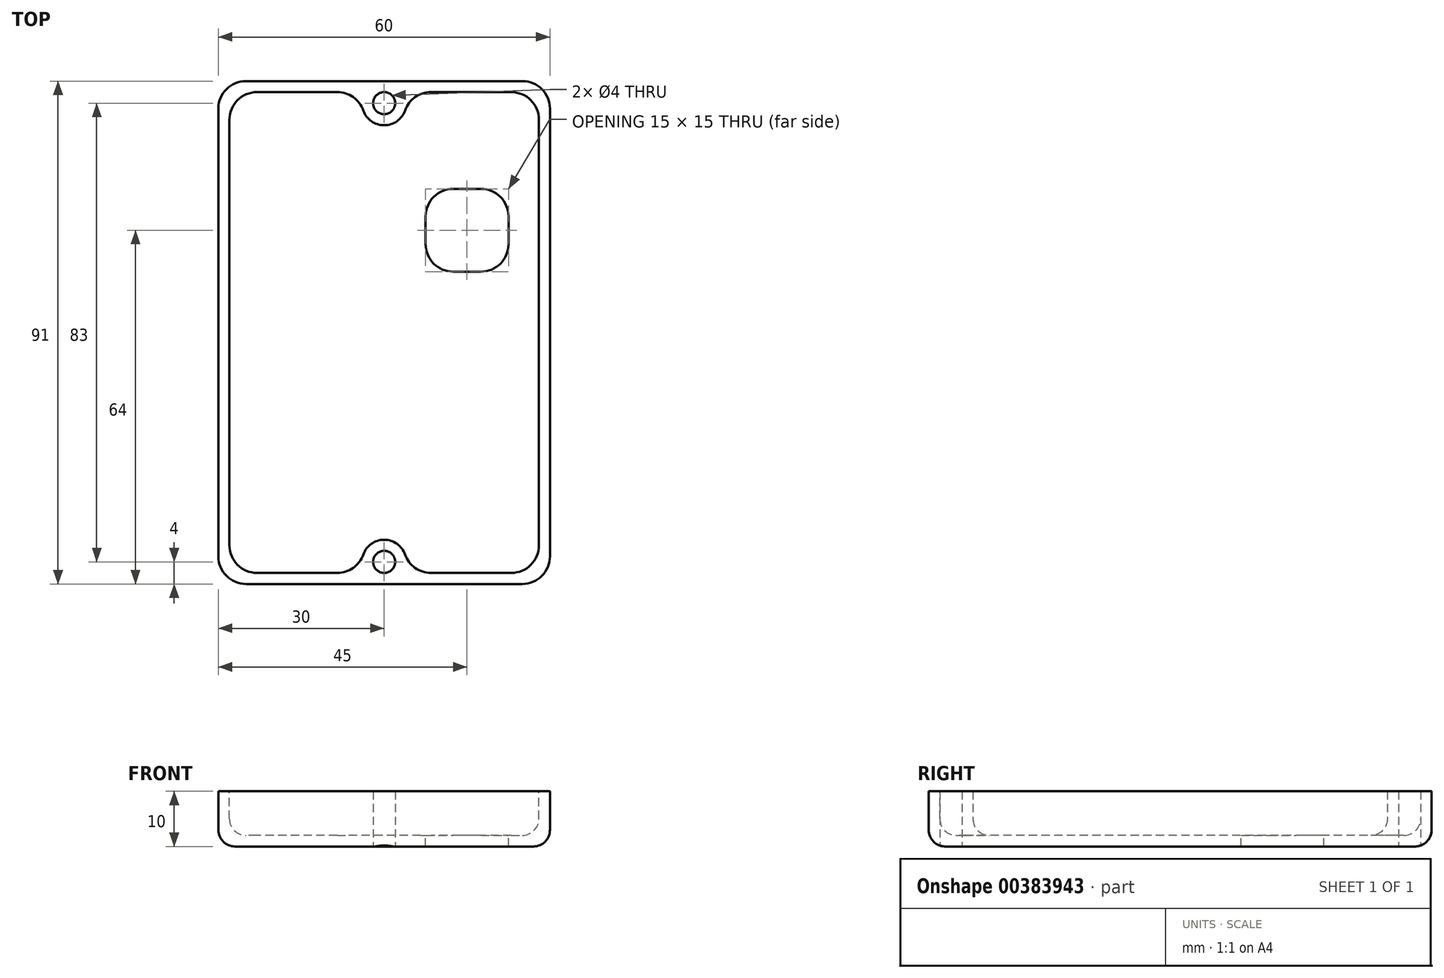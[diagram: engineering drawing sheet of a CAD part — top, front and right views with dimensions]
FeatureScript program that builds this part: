
annotation { "Feature Type Name" : "Feature", "Feature Type Description" : "" }
export const myFeature = defineFeature(function(context is Context, id is Id, definition is map)
    precondition{}
    {
        {
            assignVariable(context, id + "F0", {"name" : "lidwallthickness", "anyValue" : 2});
        }
        {
            assignVariable(context, id + "F1", {"name" : "lidheight", "anyValue" : 10});
        }
        {
            assignVariable(context, id + "F2", {"name" : "filletradius", "anyValue" : 3});
        }
        {
            var Q0;
            Q0=qCreatedBy(makeId("Top.planeOp"),FACE);
            var sketch = newSketch(context, id + "F3", { "sketchPlane" : qUnion([Q0])});
            skLineSegment(sketch, "E0.bottom", {"start": v(30, 45.5) * mm, "end": v(-30, 45.5) * mm});
            skLineSegment(sketch, "E0.top", {"start": v(30, -45.5) * mm, "end": v(-30, -45.5) * mm});
            skLineSegment(sketch, "E0.left", {"start": v(30, 45.5) * mm, "end": v(30, -45.5) * mm});
            skLineSegment(sketch, "E0.right", {"start": v(-30, 45.5) * mm, "end": v(-30, -45.5) * mm});
            skPoint(sketch, "E0.middle", {"position": v(0, 0) * mm});
            skSolve(sketch);
        }
        {
            var Q0;
            Q0=qSketchRegion(id+"F3",true);
            extrude(context, id + "F4", {"entities" : qUnion([Q0]), "depth" : (getVariable(context, 'lidheight')) * mm});
        }
        {
            var Q0;
            Q0=makeQuery(id+"F4.opExtrude","CAP_FACE",FACE,{"disambiguationData":[OSD([sQuery(id+"F3.wireOp",EDGE,"E0.bottom"),sQuery(id+"F3.wireOp",EDGE,"E0.top"),sQuery(id+"F3.wireOp",EDGE,"E0.left"),sQuery(id+"F3.wireOp",EDGE,"E0.right")])],"isStart":false});
            var sketch = newSketch(context, id + "F5", { "sketchPlane" : qUnion([Q0])});
            skLineSegment(sketch, "E1.bottom", {"start": v(28, 43.5) * mm, "end": v(-28, 43.5) * mm});
            skLineSegment(sketch, "E1.top", {"start": v(28, -43.5) * mm, "end": v(-28, -43.5) * mm});
            skLineSegment(sketch, "E1.left", {"start": v(28, 43.5) * mm, "end": v(28, -43.5) * mm});
            skLineSegment(sketch, "E1.right", {"start": v(-28, 43.5) * mm, "end": v(-28, -43.5) * mm});
            skPoint(sketch, "E1.middle", {"position": v(0, 0) * mm});
            skSolve(sketch);
        }
        {
            var Q0;
            Q0=qSketchRegion(id+"F5",true);
            extrude(context, id + "F6", {"entities" : qUnion([Q0]), "operationType" : NewBodyOperationType.REMOVE, "oppositeDirection" : true, "depth" : (getVariable(context, 'lidheight') - getVariable(context, 'lidwallthickness')) * mm});
        }
        {
            var Q0;
            Q0=makeQuery(id+"F4.opExtrude","CAP_FACE",FACE,{"disambiguationData":[OSD([sQuery(id+"F3.wireOp",EDGE,"E0.bottom"),sQuery(id+"F3.wireOp",EDGE,"E0.top"),sQuery(id+"F3.wireOp",EDGE,"E0.left"),sQuery(id+"F3.wireOp",EDGE,"E0.right")])],"isStart":true});
            var sketch = newSketch(context, id + "F7", { "sketchPlane" : qUnion([Q0])});
            skCircle(sketch, "E2", {"center": v(0, -41.5) * mm, "radius": 4 * mm});
            skCircle(sketch, "E3.MirrorC", {"center": v(0, 41.5) * mm, "radius": 4 * mm});
            skSolve(sketch);
        }
        {
            var Q0;
            Q0=qSketchRegion(id+"F7",true);
            extrude(context, id + "F8", {"entities" : qUnion([Q0]), "operationType" : NewBodyOperationType.ADD, "oppositeDirection" : true, "depth" : (getVariable(context, 'lidheight')) * mm});
        }
        {
            var Q0;
            Q0=makeQuery(id+"F4.opExtrude","CAP_FACE",FACE,{"disambiguationData":[OSD([sQuery(id+"F3.wireOp",EDGE,"E0.bottom"),sQuery(id+"F3.wireOp",EDGE,"E0.top"),sQuery(id+"F3.wireOp",EDGE,"E0.left"),sQuery(id+"F3.wireOp",EDGE,"E0.right")])],"isStart":true});
            var sketch = newSketch(context, id + "F9", { "sketchPlane" : qUnion([Q0])});
            skCircle(sketch, "E4", {"center": v(0, -41.5) * mm, "radius": 2 * mm});
            skPoint(sketch, "E4.centerSnap0", {"position": v(0, -45.5) * mm});
            skCircle(sketch, "E5.MirrorC", {"center": v(0, 41.5) * mm, "radius": 2 * mm});
            skSolve(sketch);
        }
        {
            var Q0;
            Q0=qSketchRegion(id+"F9",true);
            extrude(context, id + "F10", {"entities" : qUnion([Q0]), "operationType" : NewBodyOperationType.REMOVE, "endBound" : BoundingType.THROUGH_ALL, "oppositeDirection" : true, "depth" : 25 * mm});
        }
        {
            var Q0;
            Q0=makeQuery(id+"F8.boolean.opBoolean","INTERSECT",EDGE,{"disambiguationData":[OD(1.0)],"derivedFrom":[makeQuery(id+"F6.boolean.opBoolean","COPY",FACE,{"derivedFrom":makeQuery(id+"F6.opExtrude","SWEPT_FACE",FACE,{"disambiguationData":[OSD([sQuery(id+"F5.wireOp",EDGE,"E1.bottom")])]})}),makeQuery(id+"F8.opExtrude","SWEPT_FACE",FACE,{"disambiguationData":[OSD([sQuery(id+"F7.wireOp",EDGE,"E2")])]})]});
            var Q1;
            Q1=makeQuery(id+"F8.boolean.opBoolean","INTERSECT",EDGE,{"disambiguationData":[OD(0.0)],"derivedFrom":[makeQuery(id+"F6.boolean.opBoolean","COPY",FACE,{"derivedFrom":makeQuery(id+"F6.opExtrude","SWEPT_FACE",FACE,{"disambiguationData":[OSD([sQuery(id+"F5.wireOp",EDGE,"E1.bottom")])]})}),makeQuery(id+"F8.opExtrude","SWEPT_FACE",FACE,{"disambiguationData":[OSD([sQuery(id+"F7.wireOp",EDGE,"E2")])]})]});
            var Q2;
            Q2=makeQuery(id+"F8.boolean.opBoolean","INTERSECT",EDGE,{"disambiguationData":[OD(0.0)],"derivedFrom":[makeQuery(id+"F6.boolean.opBoolean","COPY",FACE,{"derivedFrom":makeQuery(id+"F6.opExtrude","SWEPT_FACE",FACE,{"disambiguationData":[OSD([sQuery(id+"F5.wireOp",EDGE,"E1.top")])]})}),makeQuery(id+"F8.opExtrude","SWEPT_FACE",FACE,{"disambiguationData":[OSD([sQuery(id+"F7.wireOp",EDGE,"E3.MirrorC")])]})]});
            var Q3;
            Q3=makeQuery(id+"F8.boolean.opBoolean","INTERSECT",EDGE,{"disambiguationData":[OD(1.0)],"derivedFrom":[makeQuery(id+"F6.boolean.opBoolean","COPY",FACE,{"derivedFrom":makeQuery(id+"F6.opExtrude","SWEPT_FACE",FACE,{"disambiguationData":[OSD([sQuery(id+"F5.wireOp",EDGE,"E1.top")])]})}),makeQuery(id+"F8.opExtrude","SWEPT_FACE",FACE,{"disambiguationData":[OSD([sQuery(id+"F7.wireOp",EDGE,"E3.MirrorC")])]})]});
            fillet(context, id + "F11", {"entities" : qUnion([Q0, Q1, Q2, Q3]), "radius" : 5 * mm, "tangentPropagation" : true, "allowEdgeOverflow" : false});
        }
        {
            var Q0;
            Q0=makeQuery(id+"F4.opExtrude","SWEPT_EDGE",EDGE,{"disambiguationData":[OSD([sQuery(id+"F3.wireOp",EDGE,"E0.top"),sQuery(id+"F3.wireOp",EDGE,"E0.left")])]});
            var Q1;
            Q1=makeQuery(id+"F4.opExtrude","SWEPT_EDGE",EDGE,{"disambiguationData":[OSD([sQuery(id+"F3.wireOp",EDGE,"E0.top"),sQuery(id+"F3.wireOp",EDGE,"E0.right")])]});
            var Q2;
            Q2=makeQuery(id+"F4.opExtrude","SWEPT_EDGE",EDGE,{"disambiguationData":[OSD([sQuery(id+"F3.wireOp",EDGE,"E0.bottom"),sQuery(id+"F3.wireOp",EDGE,"E0.left")])]});
            var Q3;
            Q3=makeQuery(id+"F4.opExtrude","SWEPT_EDGE",EDGE,{"disambiguationData":[OSD([sQuery(id+"F3.wireOp",EDGE,"E0.bottom"),sQuery(id+"F3.wireOp",EDGE,"E0.right")])]});
            var Q4;
            Q4=makeQuery(id+"F6.boolean.opBoolean","COPY",EDGE,{"derivedFrom":makeQuery(id+"F6.opExtrude","SWEPT_EDGE",EDGE,{"disambiguationData":[OSD([sQuery(id+"F5.wireOp",EDGE,"E1.top"),sQuery(id+"F5.wireOp",EDGE,"E1.left")])]})});
            var Q5;
            Q5=makeQuery(id+"F6.boolean.opBoolean","COPY",EDGE,{"derivedFrom":makeQuery(id+"F6.opExtrude","SWEPT_EDGE",EDGE,{"disambiguationData":[OSD([sQuery(id+"F5.wireOp",EDGE,"E1.top"),sQuery(id+"F5.wireOp",EDGE,"E1.right")])]})});
            var Q6;
            Q6=makeQuery(id+"F6.boolean.opBoolean","COPY",EDGE,{"derivedFrom":makeQuery(id+"F6.opExtrude","SWEPT_EDGE",EDGE,{"disambiguationData":[OSD([sQuery(id+"F5.wireOp",EDGE,"E1.bottom"),sQuery(id+"F5.wireOp",EDGE,"E1.right")])]})});
            var Q7;
            Q7=makeQuery(id+"F6.boolean.opBoolean","COPY",EDGE,{"derivedFrom":makeQuery(id+"F6.opExtrude","SWEPT_EDGE",EDGE,{"disambiguationData":[OSD([sQuery(id+"F5.wireOp",EDGE,"E1.bottom"),sQuery(id+"F5.wireOp",EDGE,"E1.left")])]})});
            fillet(context, id + "F12", {"entities" : qUnion([Q0, Q1, Q2, Q3, Q4, Q5, Q6, Q7]), "radius" : 5 * mm, "tangentPropagation" : true, "allowEdgeOverflow" : false});
        }
        {
            var Q0;
            Q0=makeQuery(id+"F6.boolean.opBoolean","COPY",EDGE,{"derivedFrom":makeQuery(id+"F6.opExtrude","CAP_EDGE",EDGE,{"disambiguationData":[OSD([sQuery(id+"F5.wireOp",EDGE,"E1.right")])],"isStart":false})});
            var Q1;
            Q1=makeQuery(id+"F4.opExtrude","CAP_EDGE",EDGE,{"disambiguationData":[OSD([sQuery(id+"F3.wireOp",EDGE,"E0.left")])],"isStart":true});
            fillet(context, id + "F13", {"entities" : qUnion([Q0, Q1]), "radius" : (getVariable(context, 'filletradius')) * mm, "tangentPropagation" : true, "allowEdgeOverflow" : false});
        }
        {
            var Q0;
            Q0=makeQuery(id+"F6.boolean.opBoolean","COPY",FACE,{"derivedFrom":makeQuery(id+"F6.opExtrude","CAP_FACE",FACE,{"disambiguationData":[OSD([sQuery(id+"F5.wireOp",EDGE,"E1.bottom"),sQuery(id+"F5.wireOp",EDGE,"E1.top"),sQuery(id+"F5.wireOp",EDGE,"E1.left"),sQuery(id+"F5.wireOp",EDGE,"E1.right")])],"isStart":false})});
            var sketch = newSketch(context, id + "F14", { "sketchPlane" : qUnion([Q0])});
            skLineSegment(sketch, "E6.bottom", {"start": v(22.5, 11) * mm, "end": v(7.5, 11) * mm});
            skLineSegment(sketch, "E6.top", {"start": v(22.5, 26) * mm, "end": v(7.5, 26) * mm});
            skLineSegment(sketch, "E6.left", {"start": v(22.5, 11) * mm, "end": v(22.5, 26) * mm});
            skLineSegment(sketch, "E6.right", {"start": v(7.5, 11) * mm, "end": v(7.5, 26) * mm});
            skPoint(sketch, "E6.middle", {"position": v(15, 18.5) * mm});
            skSolve(sketch);
        }
        {
            var Q0;
            Q0=makeQuery(id+"F14.imprint","IMPRINT",FACE,{"disambiguationData":[TD([[makeQuery(id+"F14.imprint","IMPRINT",EDGE,{"derivedFrom":sQuery(id+"F14.wireOp",EDGE,"E6.bottom")}),-1.0]])]});
            extrude(context, id + "F15", {"entities" : qUnion([Q0]), "operationType" : NewBodyOperationType.REMOVE, "endBound" : BoundingType.THROUGH_ALL, "oppositeDirection" : true, "depth" : 25 * mm});
        }
        {
            var Q0;
            Q0=makeQuery(id+"F15.boolean.opBoolean","COPY",EDGE,{"derivedFrom":makeQuery(id+"F15.opExtrude","SWEPT_EDGE",EDGE,{"disambiguationData":[OSD([sQuery(id+"F14.wireOp",EDGE,"E6.top"),sQuery(id+"F14.wireOp",EDGE,"E6.right")])]})});
            var Q1;
            Q1=makeQuery(id+"F15.boolean.opBoolean","COPY",EDGE,{"derivedFrom":makeQuery(id+"F15.opExtrude","SWEPT_EDGE",EDGE,{"disambiguationData":[OSD([sQuery(id+"F14.wireOp",EDGE,"E6.top"),sQuery(id+"F14.wireOp",EDGE,"E6.left")])]})});
            var Q2;
            Q2=makeQuery(id+"F15.boolean.opBoolean","COPY",EDGE,{"derivedFrom":makeQuery(id+"F15.opExtrude","SWEPT_EDGE",EDGE,{"disambiguationData":[OSD([sQuery(id+"F14.wireOp",EDGE,"E6.bottom"),sQuery(id+"F14.wireOp",EDGE,"E6.left")])]})});
            var Q3;
            Q3=makeQuery(id+"F15.boolean.opBoolean","COPY",EDGE,{"derivedFrom":makeQuery(id+"F15.opExtrude","SWEPT_EDGE",EDGE,{"disambiguationData":[OSD([sQuery(id+"F14.wireOp",EDGE,"E6.bottom"),sQuery(id+"F14.wireOp",EDGE,"E6.right")])]})});
            fillet(context, id + "F16", {"entities" : qUnion([Q0, Q1, Q2, Q3]), "radius" : 5 * mm, "tangentPropagation" : true, "allowEdgeOverflow" : false});
        }
    });
